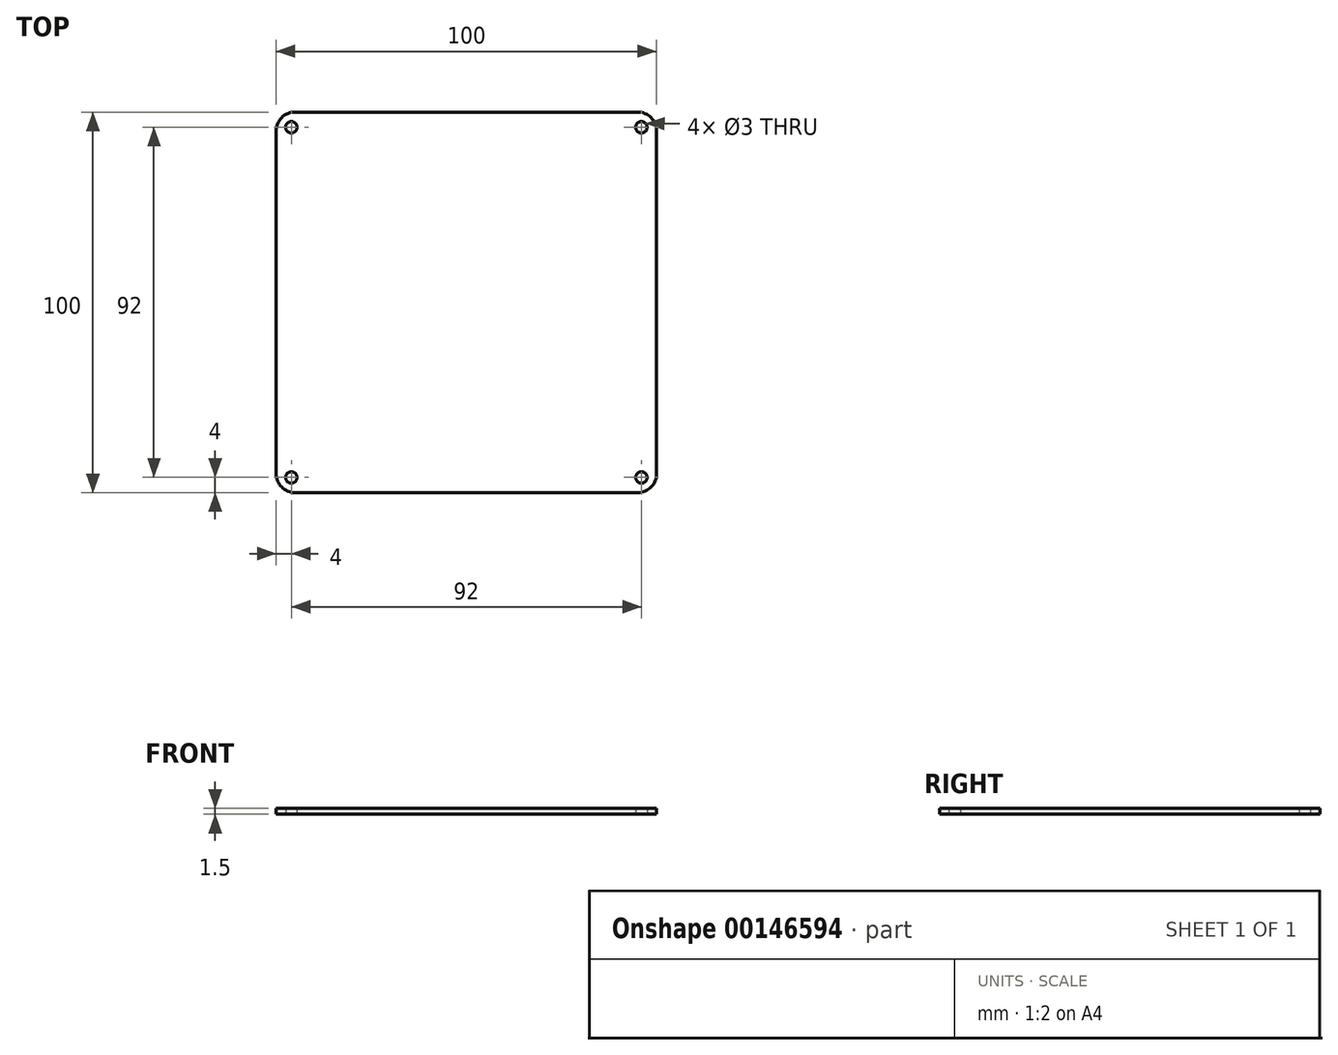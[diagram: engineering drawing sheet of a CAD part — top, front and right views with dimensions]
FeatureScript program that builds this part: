
annotation { "Feature Type Name" : "Feature", "Feature Type Description" : "" }
export const myFeature = defineFeature(function(context is Context, id is Id, definition is map)
    precondition{}
    {
        {
            var Q0;
            Q0=qCreatedBy(makeId("Top.planeOp"),FACE);
            var sketch = newSketch(context, id + "F0", { "sketchPlane" : qUnion([Q0])});
            skLineSegment(sketch, "E0.bottom", {"start": v(5, 0) * mm, "end": v(95, 0) * mm});
            skLineSegment(sketch, "E0.top", {"start": v(5, 100) * mm, "end": v(95, 100) * mm});
            skLineSegment(sketch, "E0.left", {"start": v(0, 5) * mm, "end": v(0, 95) * mm});
            skLineSegment(sketch, "E0.right", {"start": v(100, 5) * mm, "end": v(100, 95) * mm});
            skCircle(sketch, "E1", {"center": v(4, 96) * mm, "radius": 1.5 * mm});
            skCircle(sketch, "E2", {"center": v(96, 96) * mm, "radius": 1.5 * mm});
            skCircle(sketch, "E3", {"center": v(96, 4) * mm, "radius": 1.5 * mm});
            skCircle(sketch, "E4", {"center": v(4, 4) * mm, "radius": 1.5 * mm});
            skPoint(sketch, "E5.visualSharp", {"position": v(0, 100) * mm});
            skArc(sketch, "E5.filletArc", {"start": v(5, 100) * mm, "mid": v(1.46, 98.54) * mm, "end": v(0, 95) * mm});
            skPoint(sketch, "E6.visualSharp", {"position": v(100, 100) * mm});
            skArc(sketch, "E6.filletArc", {"start": v(100, 95) * mm, "mid": v(98.54, 98.54) * mm, "end": v(95, 100) * mm});
            skPoint(sketch, "E7.visualSharp", {"position": v(100, 0) * mm});
            skArc(sketch, "E7.filletArc", {"start": v(95, 0) * mm, "mid": v(98.54, 1.46) * mm, "end": v(100, 5) * mm});
            skPoint(sketch, "E8.visualSharp", {"position": v(0, 0) * mm});
            skArc(sketch, "E8.filletArc", {"start": v(0, 5) * mm, "mid": v(1.46, 1.46) * mm, "end": v(5, 0) * mm});
            skSolve(sketch);
        }
        {
            var Q0;
            Q0 = qSketchRegion(id + "F0", true);
            extrude(context, id + "F1", {"entities" : qUnion([Q0]), "depth" : 1.5 * mm});
        }
    });
